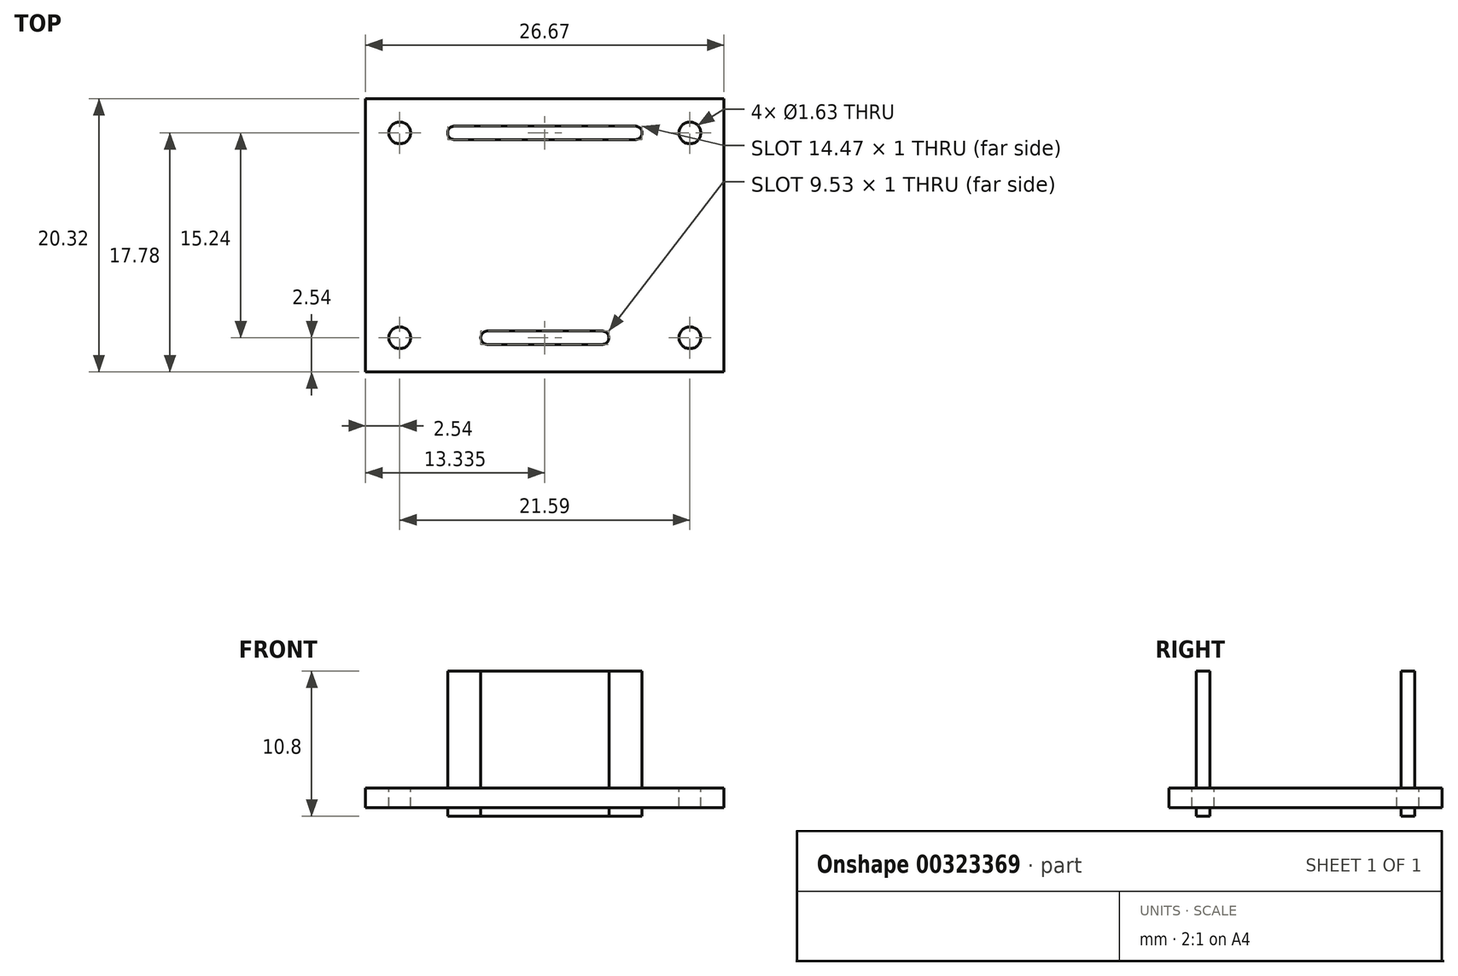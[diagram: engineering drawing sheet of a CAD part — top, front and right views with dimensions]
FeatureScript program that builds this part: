
annotation { "Feature Type Name" : "Feature", "Feature Type Description" : "" }
export const myFeature = defineFeature(function(context is Context, id is Id, definition is map)
    precondition{}
    {
        {
            var Q0;
            Q0=qCreatedBy(makeId("Top.planeOp"),FACE);
            var sketch = newSketch(context, id + "F0", { "sketchPlane" : qUnion([Q0])});
            skLineSegment(sketch, "E0.bottom", {"start": v(0, 0) * mm, "end": v(26.67, 0) * mm});
            skLineSegment(sketch, "E0.top", {"start": v(0, 20.32) * mm, "end": v(26.67, 20.32) * mm});
            skLineSegment(sketch, "E0.left", {"start": v(0, 0) * mm, "end": v(0, 20.32) * mm});
            skLineSegment(sketch, "E0.right", {"start": v(26.67, 0) * mm, "end": v(26.67, 20.32) * mm});
            skSolve(sketch);
        }
        {
            var Q0;
            Q0=makeQuery(id+"F0.imprint","IMPRINT",FACE,{"disambiguationData":[TD([[makeQuery(id+"F0.imprint","IMPRINT",EDGE,{"derivedFrom":sQuery(id+"F0.wireOp",EDGE,"E0.bottom")}),1.0]])]});
            extrude(context, id + "F1", {"entities" : qUnion([Q0]), "depth" : 1.45 * mm});
        }
        {
            var Q0;
            Q0=makeQuery(id+"F1.opExtrude","CAP_FACE",FACE,{"disambiguationData":[OSD([sQuery(id+"F0.wireOp",EDGE,"E0.bottom"),sQuery(id+"F0.wireOp",EDGE,"E0.top"),sQuery(id+"F0.wireOp",EDGE,"E0.left"),sQuery(id+"F0.wireOp",EDGE,"E0.right")])],"isStart":false});
            var sketch = newSketch(context, id + "F2", { "sketchPlane" : qUnion([Q0])});
            skLineSegment(sketch, "E1.0", {"start": v(2.54, 17.78) * mm, "end": v(24.13, 17.78) * mm, "construction": true});
            skLineSegment(sketch, "E1.1", {"start": v(2.54, 2.54) * mm, "end": v(2.54, 17.78) * mm, "construction": true});
            skLineSegment(sketch, "E1.2", {"start": v(2.54, 2.54) * mm, "end": v(24.13, 2.54) * mm, "construction": true});
            skLineSegment(sketch, "E1.3", {"start": v(24.13, 2.54) * mm, "end": v(24.13, 17.78) * mm, "construction": true});
            skSolve(sketch);
        }
        {
            var Q0;
            Q0=sQuery(id+"F2.wireOp",VERTEX,"E1.1.end");
            var Q1;
            Q1=sQuery(id+"F2.wireOp",VERTEX,"E1.2.start");
            var Q2;
            Q2=sQuery(id+"F2.wireOp",VERTEX,"E1.3.start");
            var Q3;
            Q3=sQuery(id+"F2.wireOp",VERTEX,"E1.0.end");
            var Q4;
            Q4=makeQuery(id+"F1.opExtrude","SWEPT_BODY",BODY,{"disambiguationData":[OSD([sQuery(id+"F0.wireOp",EDGE,"E0.bottom"),sQuery(id+"F0.wireOp",EDGE,"E0.top"),sQuery(id+"F0.wireOp",EDGE,"E0.left"),sQuery(id+"F0.wireOp",EDGE,"E0.right")])]});
            hole(context, id + "F3", {"style" : HoleStyle.SIMPLE, "endStyle" : HoleEndStyle.THROUGH, "standardTappedOrClearance" : lookupTablePath({ "standard" : "ANSI", "fit" : "Close", "size" : "#0", "type" : "Clearance" }), "standardBlindInLast" : lookupTablePath({ "fit" : "Close", "standard" : "ANSI", "size" : "#0", "type" : "Clearance" }), "holeDiameter" : 1.63 * mm, "isTappedThrough" : true, "tappedDepth" : 12.7 * mm, "tapClearance" : 3, "locations" : qUnion([Q0, Q1, Q2, Q3]), "scope" : qUnion([Q4])});
        }
        {
            var Q0;
            Q0=makeQuery(id+"F1.opExtrude","CAP_FACE",FACE,{"disambiguationData":[OSD([sQuery(id+"F0.wireOp",EDGE,"E0.bottom"),sQuery(id+"F0.wireOp",EDGE,"E0.top"),sQuery(id+"F0.wireOp",EDGE,"E0.left"),sQuery(id+"F0.wireOp",EDGE,"E0.right")])],"isStart":false});
            var sketch = newSketch(context, id + "F4", { "sketchPlane" : qUnion([Q0])});
            skLineSegment(sketch, "E2", {"start": v(2.54, 17.78) * mm, "end": v(24.13, 17.78) * mm, "construction": true});
            skLineSegment(sketch, "E3", {"start": v(6.6, 18.28) * mm, "end": v(20.07, 18.28) * mm});
            skLineSegment(sketch, "E4", {"start": v(6.6, 17.28) * mm, "end": v(20.07, 17.28) * mm});
            skLineSegment(sketch, "E5", {"start": v(6.6, 18.28) * mm, "end": v(0, 18.28) * mm, "construction": true});
            skLineSegment(sketch, "E6", {"start": v(20.07, 18.28) * mm, "end": v(26.67, 18.28) * mm, "construction": true});
            skLineSegment(sketch, "E7", {"start": v(6.6, 18.28) * mm, "end": v(6.6, 17.28) * mm, "construction": true});
            skLineSegment(sketch, "E8", {"start": v(20.07, 18.28) * mm, "end": v(20.07, 17.28) * mm, "construction": true});
            skPoint(sketch, "E9", {"position": v(6.6, 17.78) * mm});
            skArc(sketch, "E10", {"start": v(6.6, 18.28) * mm, "mid": v(6.1, 17.78) * mm, "end": v(6.6, 17.28) * mm});
            skArc(sketch, "E11", {"start": v(20.07, 18.28) * mm, "mid": v(20.57, 17.78) * mm, "end": v(20.07, 17.28) * mm});
            skLineSegment(sketch, "E12", {"start": v(9.07, 3.04) * mm, "end": v(17.6, 3.04) * mm});
            skLineSegment(sketch, "E13", {"start": v(9.07, 2.04) * mm, "end": v(17.6, 2.04) * mm});
            skLineSegment(sketch, "E14", {"start": v(9.07, 3.04) * mm, "end": v(9.07, 2.04) * mm, "construction": true});
            skPoint(sketch, "E15", {"position": v(9.07, 2.54) * mm});
            skLineSegment(sketch, "E16", {"start": v(17.6, 3.04) * mm, "end": v(17.6, 2.04) * mm, "construction": true});
            skPoint(sketch, "E17", {"position": v(17.6, 2.54) * mm});
            skPoint(sketch, "E18", {"position": v(2.54, 2.54) * mm});
            skLineSegment(sketch, "E19", {"start": v(9.07, 2.54) * mm, "end": v(0, 2.54) * mm, "construction": true});
            skLineSegment(sketch, "E20", {"start": v(17.6, 2.54) * mm, "end": v(26.67, 2.54) * mm, "construction": true});
            skArc(sketch, "E21", {"start": v(9.07, 3.04) * mm, "mid": v(8.57, 2.54) * mm, "end": v(9.07, 2.04) * mm});
            skArc(sketch, "E22", {"start": v(17.6, 3.04) * mm, "mid": v(18.1, 2.54) * mm, "end": v(17.6, 2.04) * mm});
            skSolve(sketch);
        }
        {
            var Q0;
            Q0 = qSketchRegion(id + "F4", true);
            extrude(context, id + "F5", {"entities" : qUnion([Q0]), "operationType" : NewBodyOperationType.ADD, "depth" : 8.7 * mm});
        }
        {
            var Q0;
            Q0 = qSketchRegion(id + "F4", true);
            extrude(context, id + "F6", {"entities" : qUnion([Q0]), "operationType" : NewBodyOperationType.ADD, "oppositeDirection" : true, "depth" : 2.1 * mm});
        }
    });
